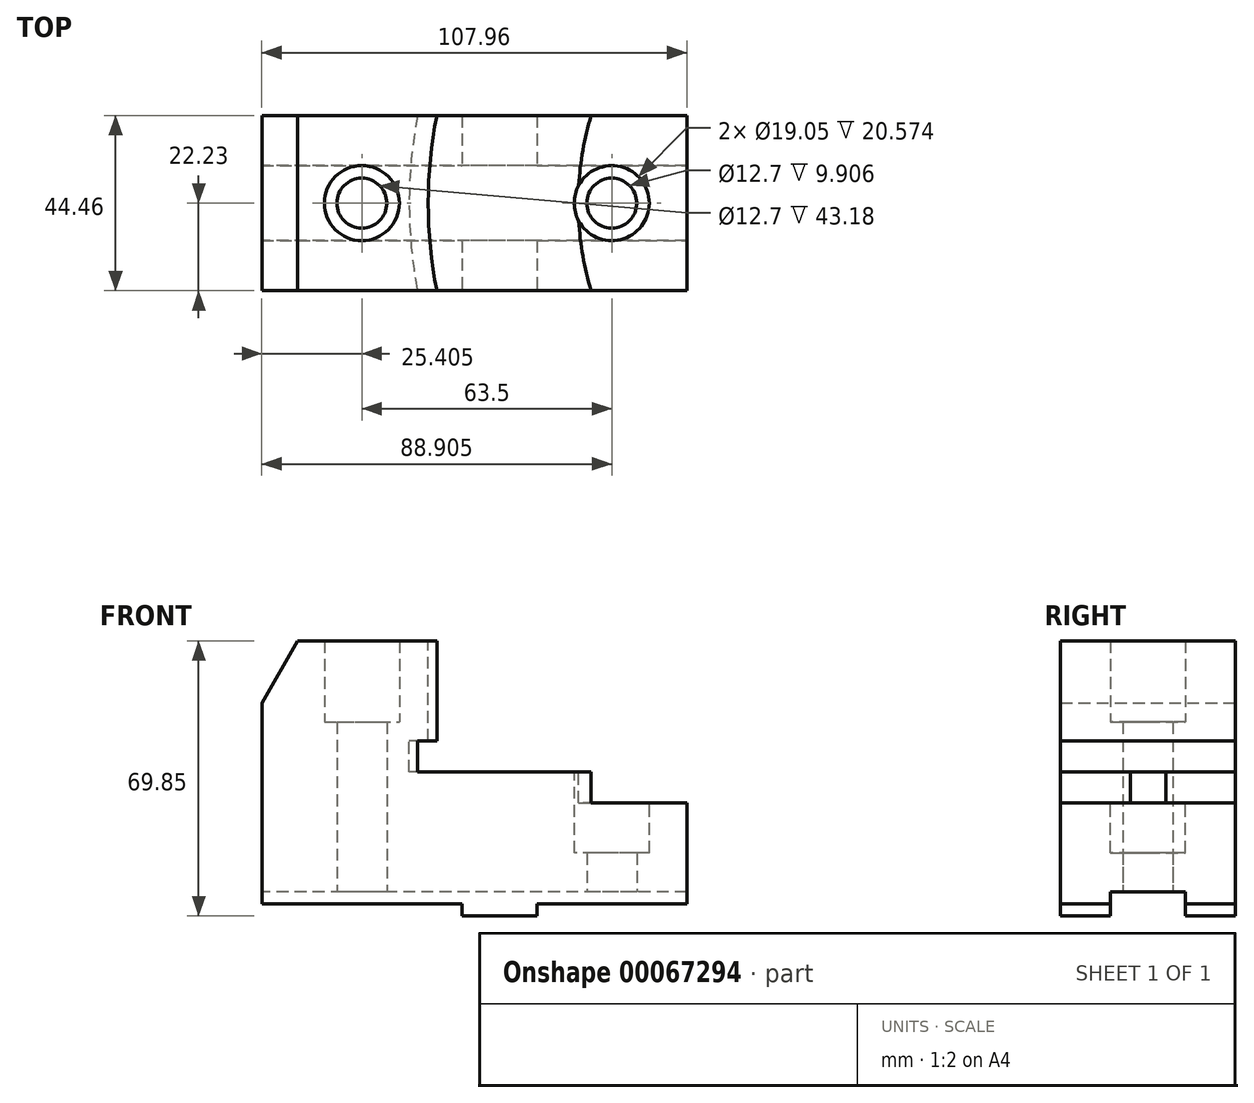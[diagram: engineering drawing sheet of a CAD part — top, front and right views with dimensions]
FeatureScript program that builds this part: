
annotation { "Feature Type Name" : "Feature", "Feature Type Description" : "" }
export const myFeature = defineFeature(function(context is Context, id is Id, definition is map)
    precondition{}
    {
        {
            var Q0;
            Q0=qCreatedBy(makeId("Front.planeOp"),FACE);
            var sketch = newSketch(context, id + "F0", { "sketchPlane" : qUnion([Q0])});
            skLineSegment(sketch, "E0.rect.bottom", {"start": v(53.98, 34.93) * mm, "end": v(-53.98, 34.93) * mm});
            skLineSegment(sketch, "E0.rect.top", {"start": v(53.98, -34.93) * mm, "end": v(-53.98, -34.93) * mm});
            skLineSegment(sketch, "E0.rect.left", {"start": v(53.98, 34.93) * mm, "end": v(53.98, -34.92) * mm});
            skLineSegment(sketch, "E0.rect.right", {"start": v(-53.98, 34.93) * mm, "end": v(-53.98, -34.93) * mm});
            skPoint(sketch, "E0.rect.middle", {"position": v(0, 0) * mm});
            skSolve(sketch);
        }
        {
            var Q0;
            Q0 = qSketchRegion(id + "F0", true);
            extrude(context, id + "F1", {"entities" : qUnion([Q0]), "depth" : 44.45 * mm, "symmetric" : true});
        }
        {
            var Q0;
            Q0=qCreatedBy(makeId("Front.planeOp"),FACE);
            var sketch = newSketch(context, id + "F2", { "sketchPlane" : qUnion([Q0])});
            skLineSegment(sketch, "E1.bottom", {"start": v(-53.98, -34.93) * mm, "end": v(-3.17, -34.93) * mm});
            skLineSegment(sketch, "E1.top", {"start": v(-53.98, -31.88) * mm, "end": v(-3.18, -31.88) * mm});
            skLineSegment(sketch, "E1.left", {"start": v(-53.98, -34.93) * mm, "end": v(-53.98, -31.88) * mm});
            skLineSegment(sketch, "E1.right", {"start": v(-3.17, -34.93) * mm, "end": v(-3.17, -31.88) * mm});
            skLineSegment(sketch, "E2.bottom", {"start": v(15.88, -31.88) * mm, "end": v(53.98, -31.88) * mm});
            skLineSegment(sketch, "E2.top", {"start": v(15.88, -34.93) * mm, "end": v(53.98, -34.93) * mm});
            skLineSegment(sketch, "E2.left", {"start": v(15.88, -31.88) * mm, "end": v(15.88, -34.93) * mm});
            skLineSegment(sketch, "E2.right", {"start": v(53.98, -31.88) * mm, "end": v(53.98, -34.92) * mm});
            skSolve(sketch);
        }
        {
            var Q0;
            Q0 = qSketchRegion(id + "F2", true);
            extrude(context, id + "F3", {"entities" : qUnion([Q0]), "operationType" : NewBodyOperationType.REMOVE, "endBound" : BoundingType.THROUGH_ALL, "oppositeDirection" : true, "depth" : 25.4 * mm, "hasSecondDirection" : true, "secondDirectionBound" : BoundingType.THROUGH_ALL, "secondDirectionOppositeDirection" : false, "secondDirectionDepth" : 25.4 * mm});
        }
        {
            var Q0;
            Q0=qCreatedBy(makeId("Right.planeOp"),FACE);
            var sketch = newSketch(context, id + "F4", { "sketchPlane" : qUnion([Q0])});
            skLineSegment(sketch, "E3.bottom", {"start": v(-9.53, -28.83) * mm, "end": v(9.52, -28.83) * mm});
            skLineSegment(sketch, "E3.top", {"start": v(-9.52, -34.93) * mm, "end": v(9.52, -34.93) * mm});
            skLineSegment(sketch, "E3.left", {"start": v(-9.53, -28.83) * mm, "end": v(-9.53, -34.93) * mm});
            skLineSegment(sketch, "E3.right", {"start": v(9.53, -28.83) * mm, "end": v(9.53, -34.93) * mm});
            skSolve(sketch);
        }
        {
            var Q0;
            Q0 = qSketchRegion(id + "F4", true);
            extrude(context, id + "F5", {"entities" : qUnion([Q0]), "operationType" : NewBodyOperationType.REMOVE, "endBound" : BoundingType.THROUGH_ALL, "depth" : 25.4 * mm, "hasSecondDirection" : true, "secondDirectionBound" : BoundingType.THROUGH_ALL, "secondDirectionOppositeDirection" : true, "secondDirectionDepth" : 25.4 * mm});
        }
        {
            var Q0;
            Q0=makeQuery(id+"F1.opExtrude","SWEPT_FACE",FACE,{"disambiguationData":[OSD([sQuery(id+"F0.wireOp",EDGE,"E0.rect.bottom")])]});
            var sketch = newSketch(context, id + "F6", { "sketchPlane" : qUnion([Q0])});
            skCircle(sketch, "E4", {"center": v(102.6, 0) * mm, "radius": 114.3 * mm});
            skPoint(sketch, "E5", {"position": v(-9.52, 22.23) * mm});
            skSolve(sketch);
        }
        {
            var Q0;
            {var subQ1=sQuery(id+"F0.wireOp",EDGE,"E0.rect.bottom");var subQ6=makeQuery(id+"F1.opExtrude","SWEPT_EDGE",EDGE,{"disambiguationData":[OSD([subQ1,sQuery(id+"F0.wireOp",EDGE,"E0.rect.left")])]});Q0=makeQuery(id+"F6.imprint","IMPRINT",FACE,{"disambiguationData":[TD([[makeQuery(id+"F6.imprint","IMPRINT",EDGE,{"derivedFrom":subQ6}),1.0]])]});}
            extrude(context, id + "F7", {"entities" : qUnion([Q0]), "operationType" : NewBodyOperationType.REMOVE, "oppositeDirection" : true, "depth" : 25.4 * mm});
        }
        {
            var Q0;
            Q0=makeQuery(id+"F7.boolean.opBoolean","COPY",FACE,{"derivedFrom":makeQuery(id+"F7.opExtrude","CAP_FACE",FACE,{"disambiguationData":[OSD([sQuery(id+"F0.wireOp",EDGE,"E0.rect.bottom"),sQuery(id+"F0.wireOp",EDGE,"E0.rect.left"),sQuery(id+"F6.wireOp",EDGE,"E4")])],"isStart":false})});
            var sketch = newSketch(context, id + "F8", { "sketchPlane" : qUnion([Q0])});
            skCircle(sketch, "E6", {"center": v(102.6, 0) * mm, "radius": 119.13 * mm});
            skSolve(sketch);
        }
        {
            var Q0;
            Q0 = qSketchRegion(id + "F8", true);
            extrude(context, id + "F9", {"entities" : qUnion([Q0]), "operationType" : NewBodyOperationType.REMOVE, "oppositeDirection" : true, "depth" : 7.87 * mm});
        }
        {
            var Q0;
            Q0=makeQuery(id+"F9.boolean.opBoolean","COPY",FACE,{"derivedFrom":makeQuery(id+"F9.opExtrude","CAP_FACE",FACE,{"disambiguationData":[OSD([sQuery(id+"F8.wireOp",EDGE,"E6")])],"isStart":false})});
            var sketch = newSketch(context, id + "F10", { "sketchPlane" : qUnion([Q0])});
            skCircle(sketch, "E7", {"center": v(102.6, 0) * mm, "radius": 76.2 * mm});
            skSolve(sketch);
        }
        {
            var Q0;
            Q0 = qSketchRegion(id + "F10", true);
            extrude(context, id + "F11", {"entities" : qUnion([Q0]), "operationType" : NewBodyOperationType.REMOVE, "oppositeDirection" : true, "depth" : 7.87 * mm});
        }
        {
            var Q0;
            Q0=makeQuery(id+"F9.boolean.opBoolean","COPY",FACE,{"derivedFrom":makeQuery(id+"F9.opExtrude","CAP_FACE",FACE,{"disambiguationData":[OSD([sQuery(id+"F8.wireOp",EDGE,"E6")])],"isStart":false})});
            var sketch = newSketch(context, id + "F12", { "sketchPlane" : qUnion([Q0])});
            skLineSegment(sketch, "E8", {"start": v(34.92, -22.23) * mm, "end": v(34.92, 22.23) * mm});
            skPoint(sketch, "E9", {"position": v(34.92, 0) * mm});
            skSolve(sketch);
        }
        {
            var Q0;
            Q0=makeQuery(id+"F1.opExtrude","SWEPT_FACE",FACE,{"disambiguationData":[OSD([sQuery(id+"F0.wireOp",EDGE,"E0.rect.bottom")])]});
            var sketch = newSketch(context, id + "F13", { "sketchPlane" : qUnion([Q0])});
            skLineSegment(sketch, "E10", {"start": v(-28.57, -22.23) * mm, "end": v(-28.58, 22.23) * mm});
            skPoint(sketch, "E11", {"position": v(-28.58, 0) * mm});
            skSolve(sketch);
        }
        {
            var Q0;
            Q0=sQuery(id+"F13.wireOp",VERTEX,"E11");
            var Q1;
            Q1=makeQuery(id+"F1.opExtrude","SWEPT_BODY",BODY,{"disambiguationData":[OSD([sQuery(id+"F0.wireOp",EDGE,"E0.rect.bottom"),sQuery(id+"F0.wireOp",EDGE,"E0.rect.top"),sQuery(id+"F0.wireOp",EDGE,"E0.rect.left"),sQuery(id+"F0.wireOp",EDGE,"E0.rect.right")])]});
            hole(context, id + "F14", {"style" : HoleStyle.C_BORE, "holeDiameter" : 12.7 * mm, "cBoreDiameter" : 19.05 * mm, "cBoreDepth" : 20.57 * mm, "endStyle" : HoleEndStyle.THROUGH, "locations" : qUnion([Q0]), "scope" : qUnion([Q1])});
        }
        {
            var Q0;
            Q0=sQuery(id+"F12.wireOp",VERTEX,"E9");
            var Q1;
            Q1=makeQuery(id+"F1.opExtrude","SWEPT_BODY",BODY,{"disambiguationData":[OSD([sQuery(id+"F0.wireOp",EDGE,"E0.rect.bottom"),sQuery(id+"F0.wireOp",EDGE,"E0.rect.top"),sQuery(id+"F0.wireOp",EDGE,"E0.rect.left"),sQuery(id+"F0.wireOp",EDGE,"E0.rect.right")])]});
            hole(context, id + "F15", {"style" : HoleStyle.SIMPLE, "holeDiameter" : 12.7 * mm, "endStyle" : HoleEndStyle.THROUGH, "locations" : qUnion([Q0]), "scope" : qUnion([Q1])});
        }
        {
            var Q0;
            Q0=makeQuery(id+"F9.boolean.opBoolean","COPY",FACE,{"derivedFrom":makeQuery(id+"F9.opExtrude","CAP_FACE",FACE,{"disambiguationData":[OSD([sQuery(id+"F8.wireOp",EDGE,"E6")])],"isStart":false})});
            var sketch = newSketch(context, id + "F16", { "sketchPlane" : qUnion([Q0])});
            skCircle(sketch, "E12", {"center": v(34.92, 0) * mm, "radius": 9.53 * mm});
            skSolve(sketch);
        }
        {
            var Q0;
            Q0 = qSketchRegion(id + "F16", true);
            extrude(context, id + "F17", {"entities" : qUnion([Q0]), "operationType" : NewBodyOperationType.REMOVE, "oppositeDirection" : true, "depth" : 20.57 * mm});
        }
        {
            var Q0;
            Q0=makeQuery(id+"F1.opExtrude","SWEPT_EDGE",EDGE,{"disambiguationData":[OSD([sQuery(id+"F0.wireOp",EDGE,"E0.rect.bottom"),sQuery(id+"F0.wireOp",EDGE,"E0.rect.right")])]});
            chamfer(context, id + "F18", {"entities" : qUnion([Q0]), "chamferType" : ChamferType.OFFSET_ANGLE, "width" : 15.75 * mm, "oppositeDirection" : false, "angle" : 30 * degree, "tangentPropagation" : true});
        }
    });
